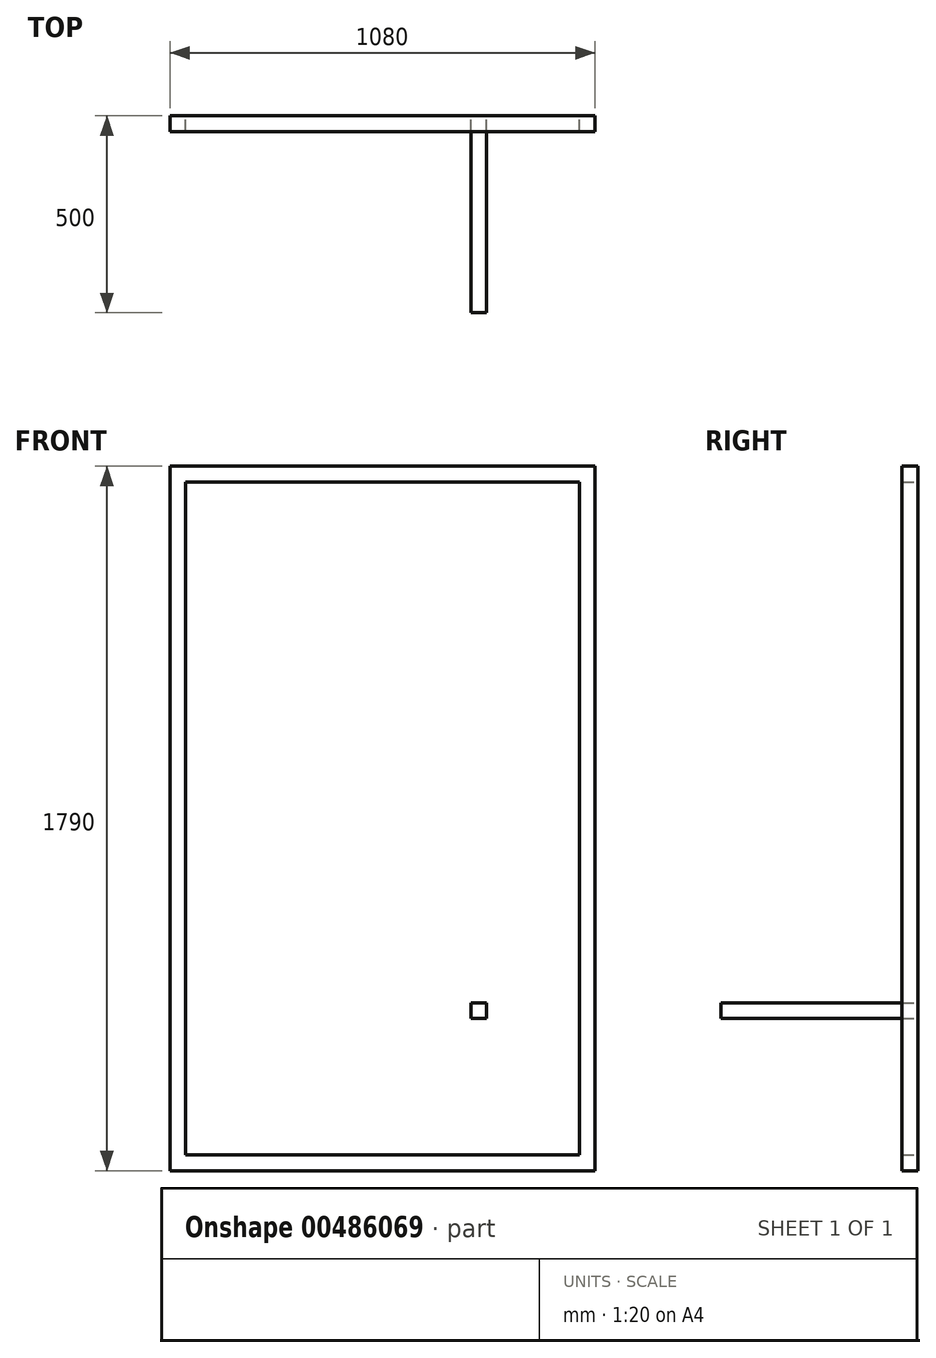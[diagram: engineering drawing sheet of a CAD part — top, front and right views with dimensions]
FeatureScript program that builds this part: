
annotation { "Feature Type Name" : "Feature", "Feature Type Description" : "" }
export const myFeature = defineFeature(function(context is Context, id is Id, definition is map)
    precondition{}
    {
        {
            var Q0;
            Q0=qCreatedBy(makeId("Front.planeOp"),FACE);
            var sketch = newSketch(context, id + "F0", { "sketchPlane" : qUnion([Q0])});
            skLineSegment(sketch, "E0.bottom", {"start": v(-80.22, 0) * mm, "end": v(999.78, 0) * mm});
            skLineSegment(sketch, "E0.top", {"start": v(-80.22, -1790) * mm, "end": v(999.78, -1790) * mm});
            skLineSegment(sketch, "E0.left", {"start": v(-80.22, 0) * mm, "end": v(-80.22, -1790) * mm});
            skLineSegment(sketch, "E0.right", {"start": v(999.78, 0) * mm, "end": v(999.78, -1790) * mm});
            skLineSegment(sketch, "E1.0", {"start": v(-80.22, -40) * mm, "end": v(999.78, -40) * mm});
            skLineSegment(sketch, "E2.0", {"start": v(959.78, -40) * mm, "end": v(959.78, -1750) * mm});
            skLineSegment(sketch, "E3.0", {"start": v(-40.22, -40) * mm, "end": v(-40.22, -1750) * mm});
            skLineSegment(sketch, "E4.0", {"start": v(-80.22, -1750) * mm, "end": v(999.78, -1750) * mm});
            skLineSegment(sketch, "E5.0", {"start": v(-38.22, -42) * mm, "end": v(957.78, -42) * mm});
            skLineSegment(sketch, "E6.0", {"start": v(-38.22, -42) * mm, "end": v(-38.22, -1748) * mm});
            skLineSegment(sketch, "E7.0", {"start": v(-38.22, -1748) * mm, "end": v(957.78, -1748) * mm});
            skLineSegment(sketch, "E8.0", {"start": v(957.78, -42) * mm, "end": v(957.78, -1748) * mm});
            skSolve(sketch);
        }
        {
            var Q0;
            Q0 = qSketchRegion(id + "F0", true);
            extrude(context, id + "F1", {"entities" : qUnion([Q0]), "depth" : 40 * mm, "offsetDistance" : 25 * mm});
        }
        {
            var Q0;
            Q0=qCreatedBy(makeId("Front.planeOp"),FACE);
            var sketch = newSketch(context, id + "F2", { "sketchPlane" : qUnion([Q0])});
            skLineSegment(sketch, "E9.bottom", {"start": v(684.34, -1403.34) * mm, "end": v(724.34, -1403.34) * mm});
            skLineSegment(sketch, "E9.top", {"start": v(684.34, -1363.34) * mm, "end": v(724.34, -1363.34) * mm});
            skLineSegment(sketch, "E9.left", {"start": v(684.34, -1403.34) * mm, "end": v(684.34, -1363.34) * mm});
            skLineSegment(sketch, "E9.right", {"start": v(724.34, -1403.34) * mm, "end": v(724.34, -1363.34) * mm});
            skSolve(sketch);
        }
        {
            var Q0;
            Q0=makeQuery(id+"F2.imprint","IMPRINT",FACE,{"disambiguationData":[TD([[makeQuery(id+"F2.imprint","IMPRINT",EDGE,{"derivedFrom":sQuery(id+"F2.wireOp",EDGE,"E9.bottom")}),1.0]])]});
            extrude(context, id + "F3", {"entities" : qUnion([Q0]), "depth" : 500 * mm, "offsetDistance" : 25 * mm});
        }
    });
